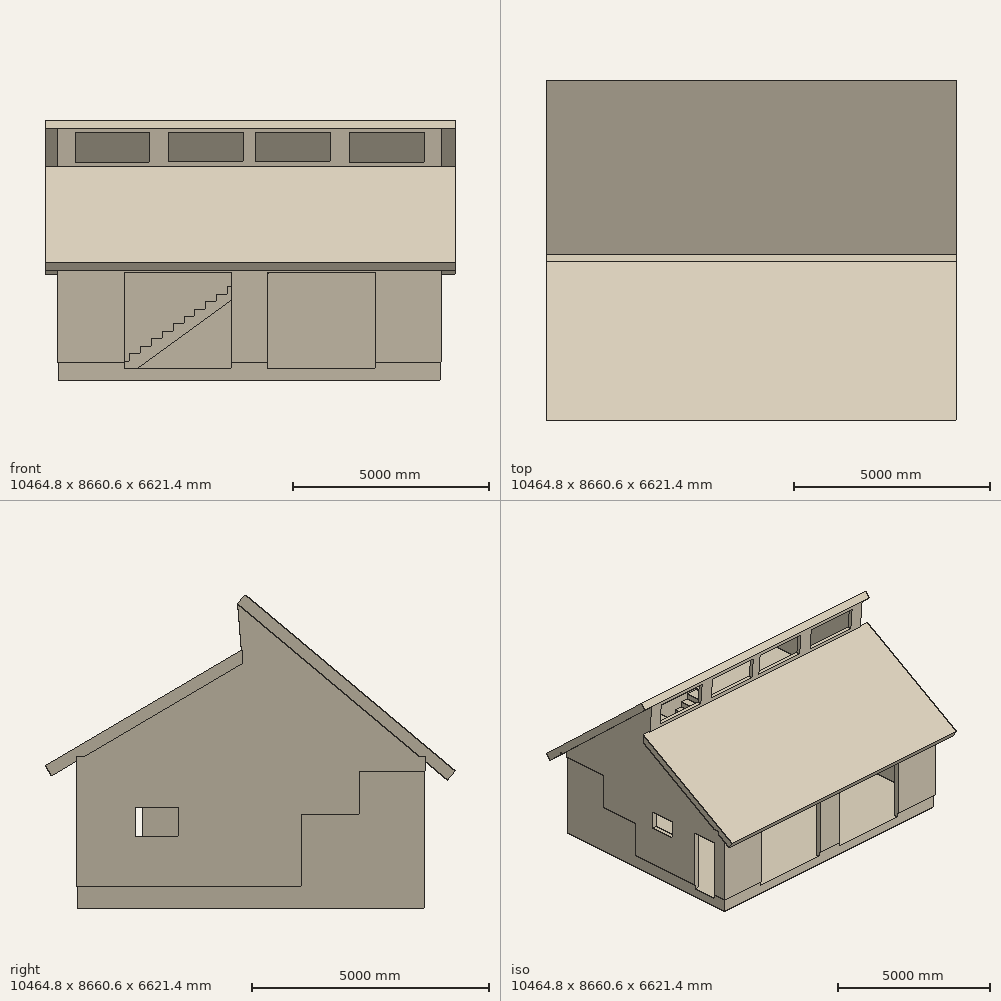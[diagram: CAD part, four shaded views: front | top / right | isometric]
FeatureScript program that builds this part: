
annotation { "Feature Type Name" : "Feature", "Feature Type Description" : "" }
export const myFeature = defineFeature(function(context is Context, id is Id, definition is map)
    precondition{}
    {
        {
            var Q0;
            Q0=qCreatedBy(makeId("Top.planeOp"),FACE);
            var sketch = newSketch(context, id + "F0", { "sketchPlane" : qUnion([Q0])});
            skLineSegment(sketch, "E0.bottom", {"start": v(0, 0) * mm, "end": v(9753.6, 0) * mm});
            skLineSegment(sketch, "E0.top", {"start": v(0, 7315.2) * mm, "end": v(9753.6, 7315.2) * mm});
            skLineSegment(sketch, "E0.left", {"start": v(0, 0) * mm, "end": v(0, 7315.2) * mm});
            skLineSegment(sketch, "E0.right", {"start": v(9753.6, 0) * mm, "end": v(9753.6, 7315.2) * mm});
            skSolve(sketch);
        }
        {
            var Q0;
            Q0=qSketchRegion(id+"F0",true);
            extrude(context, id + "F1", {"entities" : qUnion([Q0]), "depth" : 304.8 * mm});
        }
        {
            var Q0;
            Q0=makeQuery(id+"F1.opExtrude","CAP_FACE",FACE,{"disambiguationData":[OSD([sQuery(id+"F0.wireOp",EDGE,"E0.bottom"),sQuery(id+"F0.wireOp",EDGE,"E0.top"),sQuery(id+"F0.wireOp",EDGE,"E0.left"),sQuery(id+"F0.wireOp",EDGE,"E0.right")])],"isStart":false});
            var sketch = newSketch(context, id + "F2", { "sketchPlane" : qUnion([Q0])});
            skLineSegment(sketch, "E1.bottom", {"start": v(5334, 0) * mm, "end": v(4419.6, 0) * mm});
            skLineSegment(sketch, "E1.top", {"start": v(5334, 152.4) * mm, "end": v(4419.6, 152.4) * mm});
            skLineSegment(sketch, "E1.left", {"start": v(5334, 0) * mm, "end": v(5334, 152.4) * mm});
            skLineSegment(sketch, "E1.right", {"start": v(4419.6, 0) * mm, "end": v(4419.6, 152.4) * mm});
            skPoint(sketch, "E1.middle", {"position": v(4876.8, 76.2) * mm});
            skLineSegment(sketch, "E2", {"start": v(8077.2, 0) * mm, "end": v(9753.6, 0) * mm});
            skLineSegment(sketch, "E3", {"start": v(9753.6, 0) * mm, "end": v(9753.6, 7315.2) * mm});
            skLineSegment(sketch, "E4", {"start": v(9753.6, 7315.2) * mm, "end": v(0, 7315.2) * mm});
            skLineSegment(sketch, "E5", {"start": v(152.4, 7162.8) * mm, "end": v(9601.2, 7162.8) * mm});
            skLineSegment(sketch, "E6", {"start": v(9601.2, 7162.8) * mm, "end": v(9601.2, 152.4) * mm});
            skLineSegment(sketch, "E7", {"start": v(9601.2, 152.4) * mm, "end": v(8077.2, 152.4) * mm});
            skLineSegment(sketch, "E8", {"start": v(8077.2, 152.4) * mm, "end": v(8077.2, 0) * mm});
            skLineSegment(sketch, "E9", {"start": v(1676.4, 0) * mm, "end": v(1676.4, 152.4) * mm});
            skLineSegment(sketch, "E10", {"start": v(1676.4, 152.4) * mm, "end": v(152.4, 152.4) * mm});
            skLineSegment(sketch, "E11", {"start": v(152.4, 152.4) * mm, "end": v(152.4, 457.2) * mm});
            skLineSegment(sketch, "E12", {"start": v(0, 7315.2) * mm, "end": v(0, 1371.6) * mm});
            skLineSegment(sketch, "E13", {"start": v(0, 0) * mm, "end": v(1676.4, 0) * mm});
            skLineSegment(sketch, "E14", {"start": v(152.4, 457.2) * mm, "end": v(0, 457.2) * mm});
            skLineSegment(sketch, "E15", {"start": v(152.4, 1371.6) * mm, "end": v(0, 1371.6) * mm});
            skLineSegment(sketch, "E16.trimOffspring", {"start": v(152.4, 1371.6) * mm, "end": v(152.4, 7162.8) * mm});
            skLineSegment(sketch, "E17.trimOffspring", {"start": v(0, 457.2) * mm, "end": v(0, 0) * mm});
            skSolve(sketch);
        }
        {
            var Q0;
            Q0=qSketchRegion(id+"F2",true);
            extrude(context, id + "F3", {"entities" : qUnion([Q0]), "operationType" : NewBodyOperationType.ADD, "depth" : 152.4 * mm});
        }
        {
            var Q0;
            Q0=makeQuery(id+"F3.opExtrude","CAP_FACE",FACE,{"disambiguationData":[OSD([sQuery(id+"F2.wireOp",EDGE,"E2"),sQuery(id+"F2.wireOp",EDGE,"E3"),sQuery(id+"F2.wireOp",EDGE,"E4"),sQuery(id+"F2.wireOp",EDGE,"CElO2aeV-4ry8-U5nN-VFw7-lKZjGSDdjc46"),sQuery(id+"F2.wireOp",EDGE,"aXI8KXb9-mfIK-bI9D-YpWg-9FVOQ1UAsdFk"),sQuery(id+"F2.wireOp",EDGE,"YwxrfCe7-5sPB-iO6G-MdUH-hFZLTdnCo4qc"),sQuery(id+"F2.wireOp",EDGE,"E5"),sQuery(id+"F2.wireOp",EDGE,"E6"),sQuery(id+"F2.wireOp",EDGE,"E7"),sQuery(id+"F2.wireOp",EDGE,"E8")])],"isStart":false});
            var sketch = newSketch(context, id + "F4", { "sketchPlane" : qUnion([Q0])});
            skLineSegment(sketch, "E18.3", {"start": v(0, 7162.8) * mm, "end": v(9601.2, 7162.8) * mm});
            skLineSegment(sketch, "E18.4", {"start": v(0, 7315.2) * mm, "end": v(9753.6, 7315.2) * mm});
            skLineSegment(sketch, "E19", {"start": v(9753.6, 7162.8) * mm, "end": v(9753.6, 7315.2) * mm});
            skLineSegment(sketch, "E20", {"start": v(0, 7315.2) * mm, "end": v(0, 7162.8) * mm});
            skLineSegment(sketch, "E21", {"start": v(9601.2, 7162.8) * mm, "end": v(9753.6, 7162.8) * mm});
            skSolve(sketch);
        }
        {
            var Q0;
            Q0=qSketchRegion(id+"F4",true);
            extrude(context, id + "F5", {"entities" : qUnion([Q0]), "operationType" : NewBodyOperationType.ADD, "depth" : 2438.4 * mm});
        }
        {
            var Q0;
            Q0=makeQuery(id+"F5.boolean.opBoolean","MERGE",FACE,{"derivedFrom":[makeQuery(id+"F3.boolean.opBoolean","MERGE",FACE,{"derivedFrom":[makeQuery(id+"F1.opExtrude","SWEPT_FACE",FACE,{"disambiguationData":[OSD([sQuery(id+"F0.wireOp",EDGE,"E0.right")])]}),makeQuery(id+"F3.opExtrude","SWEPT_FACE",FACE,{"disambiguationData":[OSD([sQuery(id+"F2.wireOp",EDGE,"E3")])]})]}),makeQuery(id+"F5.opExtrude","SWEPT_FACE",FACE,{"disambiguationData":[OSD([sQuery(id+"F4.wireOp",EDGE,"E19")])]})]});
            var sketch = newSketch(context, id + "F6", { "sketchPlane" : qUnion([Q0])});
            skLineSegment(sketch, "E22.0", {"start": v(4724.4, 457.2) * mm, "end": v(7162.8, 457.2) * mm});
            skLineSegment(sketch, "E22.1", {"start": v(7162.8, 2895.6) * mm, "end": v(7162.8, 457.2) * mm});
            skLineSegment(sketch, "E23", {"start": v(7162.8, 2895.6) * mm, "end": v(5943.6, 2895.6) * mm});
            skLineSegment(sketch, "E24", {"start": v(5943.6, 2895.6) * mm, "end": v(5943.6, 1981.2) * mm});
            skLineSegment(sketch, "E25", {"start": v(5943.6, 1981.2) * mm, "end": v(4724.4, 1981.2) * mm});
            skLineSegment(sketch, "E26", {"start": v(4724.4, 1981.2) * mm, "end": v(4724.4, 457.2) * mm});
            skPoint(sketch, "E27.orphan", {"position": v(0, 457.2) * mm});
            skSolve(sketch);
        }
        {
            var Q0;
            Q0=qSketchRegion(id+"F6",true);
            extrude(context, id + "F7", {"entities" : qUnion([Q0]), "operationType" : NewBodyOperationType.ADD, "oppositeDirection" : true, "depth" : 152.4 * mm});
        }
        {
            var Q0;
            Q0=makeQuery(id+"F5.boolean.opBoolean","MERGE",FACE,{"derivedFrom":[makeQuery(id+"F3.boolean.opBoolean","MERGE",FACE,{"derivedFrom":[makeQuery(id+"F1.opExtrude","SWEPT_FACE",FACE,{"disambiguationData":[OSD([sQuery(id+"F0.wireOp",EDGE,"E0.left")])]}),makeQuery(id+"F3.opExtrude","SWEPT_FACE",FACE,{"disambiguationData":[OSD([sQuery(id+"F2.wireOp",EDGE,"E12")])]})]}),makeQuery(id+"F5.opExtrude","SWEPT_FACE",FACE,{"disambiguationData":[OSD([sQuery(id+"F4.wireOp",EDGE,"E20")])]})]});
            var sketch = newSketch(context, id + "F8", { "sketchPlane" : qUnion([Q0])});
            skLineSegment(sketch, "E28.0", {"start": v(-4114.8, 457.2) * mm, "end": v(-7162.8, 457.2) * mm});
            skLineSegment(sketch, "E28.1", {"start": v(-7162.8, 2895.6) * mm, "end": v(-7162.8, 457.2) * mm});
            skLineSegment(sketch, "E29", {"start": v(-7162.8, 2895.6) * mm, "end": v(-5638.8, 2895.6) * mm});
            skLineSegment(sketch, "E30", {"start": v(-5638.8, 2895.6) * mm, "end": v(-5638.8, 1676.4) * mm});
            skLineSegment(sketch, "E31", {"start": v(-5638.8, 1676.4) * mm, "end": v(-4114.8, 1676.4) * mm});
            skLineSegment(sketch, "E32", {"start": v(-4114.8, 1676.4) * mm, "end": v(-4114.8, 457.2) * mm});
            skPoint(sketch, "E33.orphan", {"position": v(-1371.6, 457.2) * mm});
            skSolve(sketch);
        }
        {
            var Q0;
            Q0=qSketchRegion(id+"F8",true);
            extrude(context, id + "F9", {"entities" : qUnion([Q0]), "operationType" : NewBodyOperationType.ADD, "oppositeDirection" : true, "depth" : 152.4 * mm});
        }
        {
            var Q0;
            Q0=makeQuery(id+"F5.boolean.opBoolean","MERGE",FACE,{"derivedFrom":[makeQuery(id+"F3.boolean.opBoolean","MERGE",FACE,{"derivedFrom":[makeQuery(id+"F1.opExtrude","SWEPT_FACE",FACE,{"disambiguationData":[OSD([sQuery(id+"F0.wireOp",EDGE,"E0.right")])]}),makeQuery(id+"F3.opExtrude","SWEPT_FACE",FACE,{"disambiguationData":[OSD([sQuery(id+"F2.wireOp",EDGE,"E3")])]})]}),makeQuery(id+"F5.opExtrude","SWEPT_FACE",FACE,{"disambiguationData":[OSD([sQuery(id+"F4.wireOp",EDGE,"E19")])]})]});
            var sketch = newSketch(context, id + "F10", { "sketchPlane" : qUnion([Q0])});
            skLineSegment(sketch, "E34.0", {"start": v(5943.6, 2895.6) * mm, "end": v(5943.6, 1981.2) * mm});
            skLineSegment(sketch, "E34.1", {"start": v(5943.6, 1981.2) * mm, "end": v(4724.4, 1981.2) * mm});
            skLineSegment(sketch, "E34.2", {"start": v(4724.4, 1981.2) * mm, "end": v(4724.4, 457.2) * mm});
            skLineSegment(sketch, "E34.3", {"start": v(0, 457.2) * mm, "end": v(4724.4, 457.2) * mm});
            skLineSegment(sketch, "E35", {"start": v(5943.6, 2895.6) * mm, "end": v(0, 2895.6) * mm});
            skLineSegment(sketch, "E36", {"start": v(0, 2895.6) * mm, "end": v(0, 457.2) * mm});
            skPoint(sketch, "E37.orphan", {"position": v(5943.6, 457.2) * mm});
            skLineSegment(sketch, "E38.bottom", {"start": v(1219.2, 2133.6) * mm, "end": v(2133.6, 2133.6) * mm});
            skLineSegment(sketch, "E38.top", {"start": v(1219.2, 1524) * mm, "end": v(2133.6, 1524) * mm});
            skLineSegment(sketch, "E38.left", {"start": v(1219.2, 2133.6) * mm, "end": v(1219.2, 1524) * mm});
            skLineSegment(sketch, "E38.right", {"start": v(2133.6, 2133.6) * mm, "end": v(2133.6, 1524) * mm});
            skSolve(sketch);
        }
        {
            var Q0;
            Q0=qSketchRegion(id+"F10",true);
            extrude(context, id + "F11", {"entities" : qUnion([Q0]), "oppositeDirection" : true, "depth" : 152.4 * mm, "hasSecondDirection" : true, "secondDirectionOppositeDirection" : false, "secondDirectionDepth" : 30.48 * mm});
        }
        {
            var Q0;
            Q0=makeQuery(id+"F3.boolean.opBoolean","MERGE",FACE,{"derivedFrom":[makeQuery(id+"F1.opExtrude","SWEPT_FACE",FACE,{"disambiguationData":[OSD([sQuery(id+"F0.wireOp",EDGE,"E0.bottom")])]}),makeQuery(id+"F3.opExtrude","SWEPT_FACE",FACE,{"disambiguationData":[OSD([sQuery(id+"F2.wireOp",EDGE,"E1.bottom")])]}),makeQuery(id+"F3.opExtrude","SWEPT_FACE",FACE,{"disambiguationData":[OSD([sQuery(id+"F2.wireOp",EDGE,"E2")])]}),makeQuery(id+"F3.opExtrude","SWEPT_FACE",FACE,{"disambiguationData":[OSD([sQuery(id+"F2.wireOp",EDGE,"E13")])]})]});
            var sketch = newSketch(context, id + "F12", { "sketchPlane" : qUnion([Q0])});
            skLineSegment(sketch, "E39.0", {"start": v(0, 457.2) * mm, "end": v(1676.4, 457.2) * mm});
            skLineSegment(sketch, "E39.2", {"start": v(4419.6, 457.2) * mm, "end": v(5334, 457.2) * mm});
            skLineSegment(sketch, "E39.3", {"start": v(8077.2, 457.2) * mm, "end": v(9753.6, 457.2) * mm});
            skLineSegment(sketch, "E39.4", {"start": v(9601.2, 457.2) * mm, "end": v(9784.08, 457.2) * mm});
            skLineSegment(sketch, "E40.1", {"start": v(9784.08, 2895.6) * mm, "end": v(9784.08, 457.2) * mm});
            skLineSegment(sketch, "E41", {"start": v(1676.4, 457.2) * mm, "end": v(1676.4, 2743.2) * mm});
            skLineSegment(sketch, "E42", {"start": v(1676.4, 2743.2) * mm, "end": v(4419.6, 2743.2) * mm});
            skLineSegment(sketch, "E43", {"start": v(4419.6, 2743.2) * mm, "end": v(4419.6, 457.2) * mm});
            skLineSegment(sketch, "E44", {"start": v(5334, 457.2) * mm, "end": v(5334, 2743.2) * mm});
            skLineSegment(sketch, "E45", {"start": v(5334, 2743.2) * mm, "end": v(8077.2, 2743.2) * mm});
            skLineSegment(sketch, "E46", {"start": v(8077.2, 2743.2) * mm, "end": v(8077.2, 457.2) * mm});
            skLineSegment(sketch, "E47", {"start": v(0, 457.2) * mm, "end": v(-30.48, 457.2) * mm});
            skLineSegment(sketch, "E48", {"start": v(-30.48, 457.2) * mm, "end": v(-30.48, 2895.6) * mm});
            skLineSegment(sketch, "E49.0", {"start": v(152.4, 2895.6) * mm, "end": v(9601.2, 2895.6) * mm});
            skLineSegment(sketch, "E50.0", {"start": v(9601.2, 2895.6) * mm, "end": v(9784.08, 2895.6) * mm});
            skLineSegment(sketch, "E51", {"start": v(-30.48, 2895.6) * mm, "end": v(152.4, 2895.6) * mm});
            skSolve(sketch);
        }
        {
            var Q0;
            Q0=qSketchRegion(id+"F12",true);
            extrude(context, id + "F13", {"entities" : qUnion([Q0]), "operationType" : NewBodyOperationType.ADD, "oppositeDirection" : true, "depth" : 152.4 * mm, "hasSecondDirection" : true, "secondDirectionOppositeDirection" : false, "secondDirectionDepth" : 30.48 * mm});
        }
        {
            var Q0;
            Q0=makeQuery(id+"F13.opExtrude","SWEPT_FACE",FACE,{"disambiguationData":[OSD([sQuery(id+"F12.wireOp",EDGE,"E48")])]});
            var sketch = newSketch(context, id + "F14", { "sketchPlane" : qUnion([Q0])});
            skLineSegment(sketch, "E52.0", {"start": v(-5638.8, 2895.6) * mm, "end": v(-5638.8, 1676.4) * mm});
            skLineSegment(sketch, "E52.1", {"start": v(-5638.8, 1676.4) * mm, "end": v(-4114.8, 1676.4) * mm});
            skLineSegment(sketch, "E52.2", {"start": v(-4114.8, 1676.4) * mm, "end": v(-4114.8, 457.2) * mm});
            skLineSegment(sketch, "E52.3", {"start": v(-1371.6, 457.2) * mm, "end": v(-4114.8, 457.2) * mm});
            skLineSegment(sketch, "E52.4", {"start": v(30.48, 457.2) * mm, "end": v(30.48, 2895.6) * mm});
            skLineSegment(sketch, "E53", {"start": v(-5638.8, 2895.6) * mm, "end": v(30.48, 2895.6) * mm});
            skLineSegment(sketch, "E54.bottom", {"start": v(-3322.32, 1828.8) * mm, "end": v(-2407.92, 1828.8) * mm});
            skLineSegment(sketch, "E54.top", {"start": v(-3322.32, 2438.4) * mm, "end": v(-2407.92, 2438.4) * mm});
            skLineSegment(sketch, "E54.left", {"start": v(-3322.32, 1828.8) * mm, "end": v(-3322.32, 2438.4) * mm});
            skLineSegment(sketch, "E54.right", {"start": v(-2407.92, 1828.8) * mm, "end": v(-2407.92, 2438.4) * mm});
            skLineSegment(sketch, "E55", {"start": v(-1371.6, 457.2) * mm, "end": v(-1371.6, 2438.4) * mm});
            skLineSegment(sketch, "E56", {"start": v(-1371.6, 2438.4) * mm, "end": v(-457.2, 2438.4) * mm});
            skLineSegment(sketch, "E57", {"start": v(-457.2, 2438.4) * mm, "end": v(-457.2, 457.2) * mm});
            skPoint(sketch, "E58.0.end.orphan", {"position": v(-1371.6, 304.8) * mm});
            skPoint(sketch, "E58.0.start.orphan", {"position": v(-1371.6, 457.2) * mm});
            skPoint(sketch, "E58.1.end.orphan", {"position": v(-457.2, 304.8) * mm});
            skLineSegment(sketch, "E59", {"start": v(-457.2, 457.2) * mm, "end": v(30.48, 457.2) * mm});
            skSolve(sketch);
        }
        {
            var Q0;
            Q0=qSketchRegion(id+"F14",true);
            extrude(context, id + "F15", {"entities" : qUnion([Q0]), "operationType" : NewBodyOperationType.ADD, "oppositeDirection" : true, "depth" : 182.88 * mm});
        }
        {
            var Q0;
            Q0=makeQuery(id+"F15.boolean.opBoolean","MERGE",FACE,{"derivedFrom":[makeQuery(id+"F13.boolean.opBoolean","MERGE",FACE,{"derivedFrom":[makeQuery(id+"F11.opExtrude","SWEPT_FACE",FACE,{"disambiguationData":[OSD([sQuery(id+"F10.wireOp",EDGE,"E35")])]}),makeQuery(id+"F13.opExtrude","SWEPT_FACE",FACE,{"disambiguationData":[OSD([sQuery(id+"F12.wireOp",EDGE,"E49.0"),sQuery(id+"F12.wireOp",EDGE,"E50.0"),sQuery(id+"F12.wireOp",EDGE,"E51")])]})]}),makeQuery(id+"F15.opExtrude","SWEPT_FACE",FACE,{"disambiguationData":[OSD([sQuery(id+"F14.wireOp",EDGE,"E53")])]})]});
            var sketch = newSketch(context, id + "F16", { "sketchPlane" : qUnion([Q0])});
            skLineSegment(sketch, "E60.bottom", {"start": v(9784.08, -30.48) * mm, "end": v(-30.48, -30.48) * mm});
            skLineSegment(sketch, "E60.top", {"start": v(9784.08, 7345.68) * mm, "end": v(-30.48, 7345.68) * mm});
            skLineSegment(sketch, "E60.left", {"start": v(9784.08, -30.48) * mm, "end": v(9784.08, 7345.68) * mm});
            skLineSegment(sketch, "E60.right", {"start": v(-30.48, -30.48) * mm, "end": v(-30.48, 7345.68) * mm});
            skLineSegment(sketch, "E61.0", {"start": v(152.4, 7162.8) * mm, "end": v(9601.2, 7162.8) * mm, "construction": true});
            skLineSegment(sketch, "E62.bottom", {"start": v(3810, 7162.8) * mm, "end": v(5842, 7162.8) * mm});
            skLineSegment(sketch, "E62.top", {"start": v(3810, 6248.4) * mm, "end": v(5842, 6248.4) * mm});
            skLineSegment(sketch, "E62.left", {"start": v(3810, 7162.8) * mm, "end": v(3810, 6248.4) * mm});
            skLineSegment(sketch, "E62.right", {"start": v(5842, 7162.8) * mm, "end": v(5842, 6248.4) * mm});
            skSolve(sketch);
        }
        {
            var Q0;
            Q0=qSketchRegion(id+"F16",true);
            extrude(context, id + "F17", {"entities" : qUnion([Q0]), "operationType" : NewBodyOperationType.ADD, "depth" : 304.8 * mm});
        }
        {
            var Q0;
            Q0=makeQuery(id+"F5.boolean.opBoolean","MERGE",FACE,{"derivedFrom":[makeQuery(id+"F3.opExtrude","SWEPT_FACE",FACE,{"disambiguationData":[OSD([sQuery(id+"F2.wireOp",EDGE,"E5")])]}),makeQuery(id+"F5.opExtrude","SWEPT_FACE",FACE,{"disambiguationData":[OSD([sQuery(id+"F4.wireOp",EDGE,"E18.3"),sQuery(id+"F4.wireOp",EDGE,"E21")])]})]});
            var sketch = newSketch(context, id + "F18", { "sketchPlane" : qUnion([Q0])});
            skLineSegment(sketch, "E63", {"start": v(1524, 304.8) * mm, "end": v(1524, 482.6) * mm});
            skLineSegment(sketch, "E64", {"start": v(1524, 482.6) * mm, "end": v(1803.4, 482.6) * mm});
            skLineSegment(sketch, "E65", {"start": v(1803.4, 482.6) * mm, "end": v(1803.4, 673.1) * mm});
            skLineSegment(sketch, "E66", {"start": v(1803.4, 673.1) * mm, "end": v(2082.8, 673.1) * mm});
            skLineSegment(sketch, "E67", {"start": v(2082.8, 673.1) * mm, "end": v(2082.8, 863.6) * mm});
            skLineSegment(sketch, "E68", {"start": v(2082.8, 863.6) * mm, "end": v(2362.2, 863.6) * mm});
            skLineSegment(sketch, "E69", {"start": v(2362.2, 863.6) * mm, "end": v(2362.2, 1054.1) * mm});
            skLineSegment(sketch, "E70", {"start": v(2362.2, 1054.1) * mm, "end": v(2641.6, 1054.1) * mm});
            skLineSegment(sketch, "E71", {"start": v(2641.6, 1054.1) * mm, "end": v(2641.6, 1244.6) * mm});
            skLineSegment(sketch, "E72", {"start": v(2641.6, 1244.6) * mm, "end": v(2921, 1244.6) * mm});
            skLineSegment(sketch, "E73", {"start": v(2921, 1244.6) * mm, "end": v(2921, 1435.1) * mm});
            skLineSegment(sketch, "E74", {"start": v(2921, 1435.1) * mm, "end": v(3200.4, 1435.1) * mm});
            skLineSegment(sketch, "E75", {"start": v(3200.4, 1435.1) * mm, "end": v(3200.4, 1625.6) * mm});
            skLineSegment(sketch, "E76", {"start": v(3200.4, 1625.6) * mm, "end": v(3479.8, 1625.6) * mm});
            skLineSegment(sketch, "E77", {"start": v(3479.8, 1625.6) * mm, "end": v(3479.8, 1816.1) * mm});
            skLineSegment(sketch, "E78", {"start": v(3479.8, 1816.1) * mm, "end": v(3759.2, 1816.1) * mm});
            skLineSegment(sketch, "E79", {"start": v(3759.2, 1816.1) * mm, "end": v(3759.2, 2006.6) * mm});
            skLineSegment(sketch, "E80", {"start": v(3759.2, 2006.6) * mm, "end": v(4038.6, 2006.6) * mm});
            skLineSegment(sketch, "E81", {"start": v(4038.6, 2006.6) * mm, "end": v(4038.6, 2197.1) * mm});
            skLineSegment(sketch, "E82", {"start": v(4038.6, 2197.1) * mm, "end": v(4318, 2197.1) * mm});
            skLineSegment(sketch, "E83", {"start": v(4318, 2197.1) * mm, "end": v(4318, 2387.6) * mm});
            skLineSegment(sketch, "E84", {"start": v(4318, 2387.6) * mm, "end": v(4597.4, 2387.6) * mm});
            skLineSegment(sketch, "E85", {"start": v(4597.4, 2387.6) * mm, "end": v(4597.4, 2578.1) * mm});
            skLineSegment(sketch, "E86", {"start": v(4597.4, 2578.1) * mm, "end": v(4876.8, 2578.1) * mm});
            skLineSegment(sketch, "E87", {"start": v(4876.8, 2578.1) * mm, "end": v(4876.8, 2768.6) * mm});
            skLineSegment(sketch, "E88", {"start": v(4876.8, 2768.6) * mm, "end": v(5156.2, 2768.6) * mm});
            skLineSegment(sketch, "E89", {"start": v(5156.2, 2768.6) * mm, "end": v(5156.2, 2959.1) * mm});
            skLineSegment(sketch, "E90", {"start": v(5156.2, 2959.1) * mm, "end": v(5435.6, 2959.1) * mm});
            skLineSegment(sketch, "E91", {"start": v(5435.6, 2959.1) * mm, "end": v(5435.6, 3149.6) * mm});
            skLineSegment(sketch, "E92", {"start": v(1524, 304.8) * mm, "end": v(2032, 304.8) * mm});
            skLineSegment(sketch, "E93", {"start": v(2032, 304.8) * mm, "end": v(5943.6, 3149.6) * mm});
            skLineSegment(sketch, "E94", {"start": v(5943.6, 3149.6) * mm, "end": v(5435.6, 3149.6) * mm});
            skSolve(sketch);
        }
        {
            var Q0;
            Q0=qSketchRegion(id+"F18",true);
            extrude(context, id + "F19", {"entities" : qUnion([Q0]), "depth" : 914.4 * mm});
        }
        {
            var Q0;
            Q0=makeQuery(id+"F17.boolean.opBoolean","MERGE",FACE,{"derivedFrom":[makeQuery(id+"F13.opExtrude","CAP_FACE",FACE,{"disambiguationData":[OSD([sQuery(id+"F12.wireOp",EDGE,"E39.0"),sQuery(id+"F12.wireOp",EDGE,"E39.2"),sQuery(id+"F12.wireOp",EDGE,"E39.3"),sQuery(id+"F12.wireOp",EDGE,"E39.4"),sQuery(id+"F12.wireOp",EDGE,"E40.1"),sQuery(id+"F12.wireOp",EDGE,"E41"),sQuery(id+"F12.wireOp",EDGE,"E42"),sQuery(id+"F12.wireOp",EDGE,"E43"),sQuery(id+"F12.wireOp",EDGE,"E44"),sQuery(id+"F12.wireOp",EDGE,"E45"),sQuery(id+"F12.wireOp",EDGE,"E46"),sQuery(id+"F12.wireOp",EDGE,"E47"),sQuery(id+"F12.wireOp",EDGE,"E48"),sQuery(id+"F12.wireOp",EDGE,"E49.0"),sQuery(id+"F12.wireOp",EDGE,"E50.0"),sQuery(id+"F12.wireOp",EDGE,"E51")])],"isStart":true}),makeQuery(id+"F17.opExtrude","SWEPT_FACE",FACE,{"disambiguationData":[OSD([sQuery(id+"F16.wireOp",EDGE,"E60.bottom")])]})]});
            var sketch = newSketch(context, id + "F20", { "sketchPlane" : qUnion([Q0])});
            skLineSegment(sketch, "E95.0", {"start": v(0, 0) * mm, "end": v(9753.6, 0) * mm, "construction": true});
            skLineSegment(sketch, "E96", {"start": v(4876.8, 0) * mm, "end": v(4876.8, 9099.26) * mm, "construction": true});
            skLineSegment(sketch, "E97", {"start": v(4876.8, 7318.1) * mm, "end": v(-487.68, 2816.76) * mm});
            skLineSegment(sketch, "E98", {"start": v(-487.68, 2816.76) * mm, "end": v(-487.68, 3214.65) * mm});
            skLineSegment(sketch, "E99", {"start": v(-487.68, 3214.65) * mm, "end": v(4876.8, 7715.98) * mm});
            skLineSegment(sketch, "E100.MirrorCS", {"start": v(10241.28, 2816.76) * mm, "end": v(10241.28, 3214.65) * mm});
            skLineSegment(sketch, "E101.MirrorCS", {"start": v(10241.28, 3214.65) * mm, "end": v(4876.8, 7715.98) * mm});
            skLineSegment(sketch, "E102.MirrorCS", {"start": v(4876.8, 7318.1) * mm, "end": v(10241.28, 2816.76) * mm});
            skSolve(sketch);
        }
        {
            var Q0;
            Q0=makeQuery(id+"F17.boolean.opBoolean","MERGE",FACE,{"derivedFrom":[makeQuery(id+"F13.opExtrude","CAP_FACE",FACE,{"disambiguationData":[OSD([sQuery(id+"F12.wireOp",EDGE,"E39.0"),sQuery(id+"F12.wireOp",EDGE,"E39.2"),sQuery(id+"F12.wireOp",EDGE,"E39.3"),sQuery(id+"F12.wireOp",EDGE,"E39.4"),sQuery(id+"F12.wireOp",EDGE,"E40.1"),sQuery(id+"F12.wireOp",EDGE,"E41"),sQuery(id+"F12.wireOp",EDGE,"E42"),sQuery(id+"F12.wireOp",EDGE,"E43"),sQuery(id+"F12.wireOp",EDGE,"E44"),sQuery(id+"F12.wireOp",EDGE,"E45"),sQuery(id+"F12.wireOp",EDGE,"E46"),sQuery(id+"F12.wireOp",EDGE,"E47"),sQuery(id+"F12.wireOp",EDGE,"E48"),sQuery(id+"F12.wireOp",EDGE,"E49.0"),sQuery(id+"F12.wireOp",EDGE,"E50.0"),sQuery(id+"F12.wireOp",EDGE,"E51")])],"isStart":true}),makeQuery(id+"F17.opExtrude","SWEPT_FACE",FACE,{"disambiguationData":[OSD([sQuery(id+"F16.wireOp",EDGE,"E60.bottom")])]})]});
            var sketch = newSketch(context, id + "F21", { "sketchPlane" : qUnion([Q0])});
            skLineSegment(sketch, "E103.0", {"start": v(4876.8, 7318.1) * mm, "end": v(-30.48, 3200.4) * mm});
            skLineSegment(sketch, "E103.1", {"start": v(4876.8, 7318.1) * mm, "end": v(9784.08, 3200.4) * mm});
            skLineSegment(sketch, "E104.0", {"start": v(-30.48, 3200.4) * mm, "end": v(9784.08, 3200.4) * mm});
            skPoint(sketch, "E105.orphan", {"position": v(10241.28, 2816.76) * mm});
            skPoint(sketch, "E106.orphan", {"position": v(-487.68, 2816.76) * mm});
            skLineSegment(sketch, "E107", {"start": v(4876.8, 7318.1) * mm, "end": v(4876.8, 2832.57) * mm, "construction": true});
            skPoint(sketch, "E107.endSnap0", {"position": v(4876.8, 3200.4) * mm});
            skLineSegment(sketch, "E108.bottom", {"start": v(3352.8, 5029.2) * mm, "end": v(4267.2, 5029.2) * mm});
            skLineSegment(sketch, "E108.top", {"start": v(3352.8, 3810) * mm, "end": v(4267.2, 3810) * mm});
            skLineSegment(sketch, "E108.left", {"start": v(3352.8, 5029.2) * mm, "end": v(3352.8, 3810) * mm});
            skLineSegment(sketch, "E108.right", {"start": v(4267.2, 5029.2) * mm, "end": v(4267.2, 3810) * mm});
            skLineSegment(sketch, "E109.MirrorCS", {"start": v(6400.8, 5029.2) * mm, "end": v(5486.4, 5029.2) * mm});
            skLineSegment(sketch, "E110.MirrorCS", {"start": v(6400.8, 5029.2) * mm, "end": v(6400.8, 3810) * mm});
            skLineSegment(sketch, "E111.MirrorCS", {"start": v(6400.8, 3810) * mm, "end": v(5486.4, 3810) * mm});
            skLineSegment(sketch, "E112.MirrorCS", {"start": v(5486.4, 5029.2) * mm, "end": v(5486.4, 3810) * mm});
            skSolve(sketch);
        }
        {
            var Q0;
            Q0=makeQuery(id+"F17.opExtrude","SWEPT_FACE",FACE,{"disambiguationData":[OSD([sQuery(id+"F16.wireOp",EDGE,"E60.top")])]});
            var sketch = newSketch(context, id + "F22", { "sketchPlane" : qUnion([Q0])});
            skLineSegment(sketch, "E113.0", {"start": v(-9784.08, 3200.4) * mm, "end": v(-6705.6, 3200.4) * mm});
            skLineSegment(sketch, "E114.0", {"start": v(-4876.8, 7318.1) * mm, "end": v(-9784.08, 3200.4) * mm});
            skLineSegment(sketch, "E114.1", {"start": v(-4876.8, 7318.1) * mm, "end": v(30.48, 3200.4) * mm});
            skPoint(sketch, "E115.orphan", {"position": v(487.68, 2816.76) * mm});
            skPoint(sketch, "E116.orphan", {"position": v(-10241.28, 2816.76) * mm});
            skLineSegment(sketch, "E117.top", {"start": v(-5791.2, 5334) * mm, "end": v(-6705.6, 5334) * mm});
            skLineSegment(sketch, "E117.left", {"start": v(-5791.2, 3200.4) * mm, "end": v(-5791.2, 5334) * mm});
            skLineSegment(sketch, "E117.right", {"start": v(-6705.6, 3200.4) * mm, "end": v(-6705.6, 5334) * mm});
            skLineSegment(sketch, "E118", {"start": v(-4876.8, 7318.1) * mm, "end": v(-4876.8, 2411.7) * mm, "construction": true});
            skPoint(sketch, "E118.endSnap0", {"position": v(-4876.8, 2895.6) * mm});
            skLineSegment(sketch, "E119.bottom", {"start": v(-4419.6, 5334) * mm, "end": v(-3200.4, 5334) * mm});
            skLineSegment(sketch, "E119.top", {"start": v(-4419.6, 4572) * mm, "end": v(-3200.4, 4572) * mm});
            skLineSegment(sketch, "E119.left", {"start": v(-4419.6, 5334) * mm, "end": v(-4419.6, 4572) * mm});
            skLineSegment(sketch, "E119.right", {"start": v(-3200.4, 5334) * mm, "end": v(-3200.4, 4572) * mm});
            skLineSegment(sketch, "E120.trimOffspring", {"start": v(-5791.2, 3200.4) * mm, "end": v(30.48, 3200.4) * mm});
            skSolve(sketch);
        }
        {
            var Q0;
            Q0=makeQuery(id+"F17.boolean.opBoolean","MERGE",FACE,{"derivedFrom":[makeQuery(id+"F15.boolean.opBoolean","MERGE",FACE,{"derivedFrom":[makeQuery(id+"F13.opExtrude","SWEPT_FACE",FACE,{"disambiguationData":[OSD([sQuery(id+"F12.wireOp",EDGE,"E48")])]}),makeQuery(id+"F15.opExtrude","CAP_FACE",FACE,{"disambiguationData":[OSD([sQuery(id+"F14.wireOp",EDGE,"E52.0"),sQuery(id+"F14.wireOp",EDGE,"E52.1"),sQuery(id+"F14.wireOp",EDGE,"E52.2"),sQuery(id+"F14.wireOp",EDGE,"E52.3"),sQuery(id+"F14.wireOp",EDGE,"E52.4"),sQuery(id+"F14.wireOp",EDGE,"E53"),sQuery(id+"F14.wireOp",EDGE,"E54.bottom"),sQuery(id+"F14.wireOp",EDGE,"E54.top"),sQuery(id+"F14.wireOp",EDGE,"E54.left"),sQuery(id+"F14.wireOp",EDGE,"E54.right"),sQuery(id+"F14.wireOp",EDGE,"E55"),sQuery(id+"F14.wireOp",EDGE,"E56"),sQuery(id+"F14.wireOp",EDGE,"E57"),sQuery(id+"F14.wireOp",EDGE,"E59")])],"isStart":true})]}),makeQuery(id+"F17.opExtrude","SWEPT_FACE",FACE,{"disambiguationData":[OSD([sQuery(id+"F16.wireOp",EDGE,"E60.right")])]})]});
            var sketch = newSketch(context, id + "F23", { "sketchPlane" : qUnion([Q0])});
            skLineSegment(sketch, "E121", {"start": v(-7812.66, 2701.02) * mm, "end": v(-7345.68, 3092.87) * mm});
            skLineSegment(sketch, "E122", {"start": v(-7345.68, 3092.87) * mm, "end": v(-7345.68, 3200.4) * mm});
            skLineSegment(sketch, "E123", {"start": v(-7345.68, 3200.4) * mm, "end": v(-7217.53, 3200.4) * mm});
            skLineSegment(sketch, "E124", {"start": v(-7217.53, 3200.4) * mm, "end": v(-3372.41, 6426.84) * mm});
            skLineSegment(sketch, "E125", {"start": v(-3372.41, 6426.84) * mm, "end": v(-3535.68, 6621.41) * mm});
            skLineSegment(sketch, "E126", {"start": v(-3535.68, 6621.41) * mm, "end": v(-7975.93, 2895.6) * mm});
            skLineSegment(sketch, "E127", {"start": v(-7975.93, 2895.6) * mm, "end": v(-7812.66, 2701.02) * mm});
            skLineSegment(sketch, "E128", {"start": v(-3473.58, 5457.64) * mm, "end": v(684.64, 3008.26) * mm});
            skLineSegment(sketch, "E129", {"start": v(684.64, 3008.26) * mm, "end": v(555.73, 2789.4) * mm});
            skLineSegment(sketch, "E130", {"start": v(555.73, 2789.4) * mm, "end": v(30.48, 3098.8) * mm});
            skLineSegment(sketch, "E131", {"start": v(30.48, 3098.8) * mm, "end": v(30.48, 3200.4) * mm});
            skLineSegment(sketch, "E132", {"start": v(30.48, 3200.4) * mm, "end": v(-142, 3200.4) * mm});
            skLineSegment(sketch, "E133", {"start": v(-142, 3200.4) * mm, "end": v(-3473.58, 5162.85) * mm});
            skLineSegment(sketch, "E134", {"start": v(-3473.58, 5457.64) * mm, "end": v(-3473.58, 5162.85) * mm});
            skPoint(sketch, "E135.orphan", {"position": v(-4299.2, 5649.17) * mm});
            skPoint(sketch, "E136.start.orphan", {"position": v(-3839.4, 6035) * mm});
            skSolve(sketch);
        }
        {
            var Q0;
            Q0 = qSketchRegion(id + "F23", true);
            extrude(context, id + "F24", {"entities" : qUnion([Q0]), "operationType" : NewBodyOperationType.ADD, "depth" : 304.8 * mm, "hasSecondDirection" : true, "secondDirectionOppositeDirection" : true, "secondDirectionDepth" : 10160 * mm});
        }
        {
            var Q0;
            Q0=makeQuery(id+"F17.boolean.opBoolean","MERGE",FACE,{"derivedFrom":[makeQuery(id+"F15.boolean.opBoolean","MERGE",FACE,{"derivedFrom":[makeQuery(id+"F13.opExtrude","SWEPT_FACE",FACE,{"disambiguationData":[OSD([sQuery(id+"F12.wireOp",EDGE,"E48")])]}),makeQuery(id+"F15.opExtrude","CAP_FACE",FACE,{"disambiguationData":[OSD([sQuery(id+"F14.wireOp",EDGE,"E52.0"),sQuery(id+"F14.wireOp",EDGE,"E52.1"),sQuery(id+"F14.wireOp",EDGE,"E52.2"),sQuery(id+"F14.wireOp",EDGE,"E52.3"),sQuery(id+"F14.wireOp",EDGE,"E52.4"),sQuery(id+"F14.wireOp",EDGE,"E53"),sQuery(id+"F14.wireOp",EDGE,"E54.bottom"),sQuery(id+"F14.wireOp",EDGE,"E54.top"),sQuery(id+"F14.wireOp",EDGE,"E54.left"),sQuery(id+"F14.wireOp",EDGE,"E54.right"),sQuery(id+"F14.wireOp",EDGE,"E55"),sQuery(id+"F14.wireOp",EDGE,"E56"),sQuery(id+"F14.wireOp",EDGE,"E57"),sQuery(id+"F14.wireOp",EDGE,"E59")])],"isStart":true})]}),makeQuery(id+"F17.opExtrude","SWEPT_FACE",FACE,{"disambiguationData":[OSD([sQuery(id+"F16.wireOp",EDGE,"E60.right")])]})]});
            var sketch = newSketch(context, id + "F25", { "sketchPlane" : qUnion([Q0])});
            skLineSegment(sketch, "E137.0", {"start": v(-7217.53, 3200.4) * mm, "end": v(-142, 3200.4) * mm});
            skLineSegment(sketch, "E138.0", {"start": v(-7217.53, 3200.4) * mm, "end": v(-3372.41, 6426.84) * mm});
            skLineSegment(sketch, "E139.0", {"start": v(-142, 3200.4) * mm, "end": v(-3473.58, 5162.85) * mm});
            skLineSegment(sketch, "E140", {"start": v(-3372.41, 6426.84) * mm, "end": v(-3473.58, 5162.85) * mm});
            skSolve(sketch);
        }
        {
            var Q0;
            Q0 = qSketchRegion(id + "F25", true);
            extrude(context, id + "F26", {"entities" : qUnion([Q0]), "operationType" : NewBodyOperationType.ADD, "oppositeDirection" : true, "depth" : 152.4 * mm});
        }
        {
            var Q0;
            Q0=makeQuery(id+"F17.boolean.opBoolean","MERGE",FACE,{"derivedFrom":[makeQuery(id+"F13.boolean.opBoolean","MERGE",FACE,{"derivedFrom":[makeQuery(id+"F11.opExtrude","CAP_FACE",FACE,{"disambiguationData":[OSD([sQuery(id+"F10.wireOp",EDGE,"E34.0"),sQuery(id+"F10.wireOp",EDGE,"E34.1"),sQuery(id+"F10.wireOp",EDGE,"E34.2"),sQuery(id+"F10.wireOp",EDGE,"E34.3"),sQuery(id+"F10.wireOp",EDGE,"E35"),sQuery(id+"F10.wireOp",EDGE,"E36"),sQuery(id+"F10.wireOp",EDGE,"E38.bottom"),sQuery(id+"F10.wireOp",EDGE,"E38.top"),sQuery(id+"F10.wireOp",EDGE,"E38.left"),sQuery(id+"F10.wireOp",EDGE,"E38.right")])],"isStart":true}),makeQuery(id+"F13.opExtrude","SWEPT_FACE",FACE,{"disambiguationData":[OSD([sQuery(id+"F12.wireOp",EDGE,"E40.1")])]})]}),makeQuery(id+"F17.opExtrude","SWEPT_FACE",FACE,{"disambiguationData":[OSD([sQuery(id+"F16.wireOp",EDGE,"E60.left")])]})]});
            var sketch = newSketch(context, id + "F27", { "sketchPlane" : qUnion([Q0])});
            skLineSegment(sketch, "E141.0", {"start": v(7217.53, 3200.4) * mm, "end": v(142, 3200.4) * mm});
            skLineSegment(sketch, "E142.0", {"start": v(7217.53, 3200.4) * mm, "end": v(3372.41, 6426.84) * mm});
            skLineSegment(sketch, "E143.0", {"start": v(142, 3200.4) * mm, "end": v(3473.58, 5162.85) * mm});
            skLineSegment(sketch, "E144", {"start": v(3372.41, 6426.84) * mm, "end": v(3473.58, 5162.85) * mm});
            skSolve(sketch);
        }
        {
            var Q0;
            Q0 = qSketchRegion(id + "F27", true);
            extrude(context, id + "F28", {"entities" : qUnion([Q0]), "operationType" : NewBodyOperationType.ADD, "oppositeDirection" : true, "depth" : 152.4 * mm});
        }
        {
            var Q0;
            Q0=makeQuery(id+"F26.opExtrude","SWEPT_FACE",FACE,{"disambiguationData":[OSD([sQuery(id+"F25.wireOp",EDGE,"E140")])]});
            var sketch = newSketch(context, id + "F29", { "sketchPlane" : qUnion([Q0])});
            skLineSegment(sketch, "E145.0", {"start": v(9784.08, 6137.29) * mm, "end": v(9784.08, 5151.68) * mm});
            skLineSegment(sketch, "E146.0", {"start": v(-30.48, 6137.29) * mm, "end": v(-30.48, 5151.68) * mm});
            skLineSegment(sketch, "E147", {"start": v(-30.48, 6137.29) * mm, "end": v(9784.08, 6137.29) * mm});
            skLineSegment(sketch, "E148", {"start": v(9784.08, 5151.68) * mm, "end": v(-30.48, 5151.68) * mm});
            skLineSegment(sketch, "E149", {"start": v(4876.8, 5151.68) * mm, "end": v(4876.8, 7522.2) * mm, "construction": true});
            skPoint(sketch, "E149.endSnap0", {"position": v(4876.8, 6137.29) * mm});
            skLineSegment(sketch, "E150", {"start": v(-1301.1, 8944.92) * mm, "end": v(0, 8944.92) * mm});
            skLineSegment(sketch, "E151.bottom", {"start": v(426.72, 5266.38) * mm, "end": v(2331.72, 5266.38) * mm});
            skLineSegment(sketch, "E151.top", {"start": v(426.72, 6028.38) * mm, "end": v(2331.72, 6028.38) * mm});
            skLineSegment(sketch, "E151.left", {"start": v(426.72, 5266.38) * mm, "end": v(426.72, 6028.38) * mm});
            skLineSegment(sketch, "E151.right", {"start": v(2331.72, 5266.38) * mm, "end": v(2331.72, 6028.38) * mm});
            skLineSegment(sketch, "E152.bottom", {"start": v(2814.32, 6028.38) * mm, "end": v(4719.32, 6028.38) * mm});
            skLineSegment(sketch, "E152.top", {"start": v(2814.32, 5279.2) * mm, "end": v(4719.32, 5279.2) * mm});
            skLineSegment(sketch, "E152.left", {"start": v(2814.32, 6028.38) * mm, "end": v(2814.32, 5279.2) * mm});
            skLineSegment(sketch, "E152.right", {"start": v(4719.32, 6028.38) * mm, "end": v(4719.32, 5279.2) * mm});
            skLineSegment(sketch, "E153.MirrorCS", {"start": v(7421.88, 5266.38) * mm, "end": v(7421.88, 6028.38) * mm});
            skLineSegment(sketch, "E154.MirrorCS", {"start": v(9326.88, 5266.38) * mm, "end": v(9326.88, 6028.38) * mm});
            skLineSegment(sketch, "E155.MirrorCS", {"start": v(9326.88, 6028.38) * mm, "end": v(7421.88, 6028.38) * mm});
            skLineSegment(sketch, "E156.MirrorCS", {"start": v(9326.88, 5266.38) * mm, "end": v(7421.88, 5266.38) * mm});
            skLineSegment(sketch, "E157.MirrorCS", {"start": v(6939.28, 6028.38) * mm, "end": v(5034.28, 6028.38) * mm});
            skLineSegment(sketch, "E158.MirrorCS", {"start": v(6939.28, 5279.2) * mm, "end": v(5034.28, 5279.2) * mm});
            skLineSegment(sketch, "E159.MirrorCS", {"start": v(6939.28, 6028.38) * mm, "end": v(6939.28, 5279.2) * mm});
            skLineSegment(sketch, "E160.MirrorCS", {"start": v(5034.28, 6028.38) * mm, "end": v(5034.28, 5279.2) * mm});
            skLineSegment(sketch, "E161.MirrorCS", {"start": v(-30.48, 5151.68) * mm, "end": v(9784.08, 5151.68) * mm});
            skSolve(sketch);
        }
        {
            var Q0;
            Q0 = qSketchRegion(id + "F29", true);
            extrude(context, id + "F30", {"entities" : qUnion([Q0]), "operationType" : NewBodyOperationType.ADD, "oppositeDirection" : true, "depth" : 127 * mm});
        }
    });
